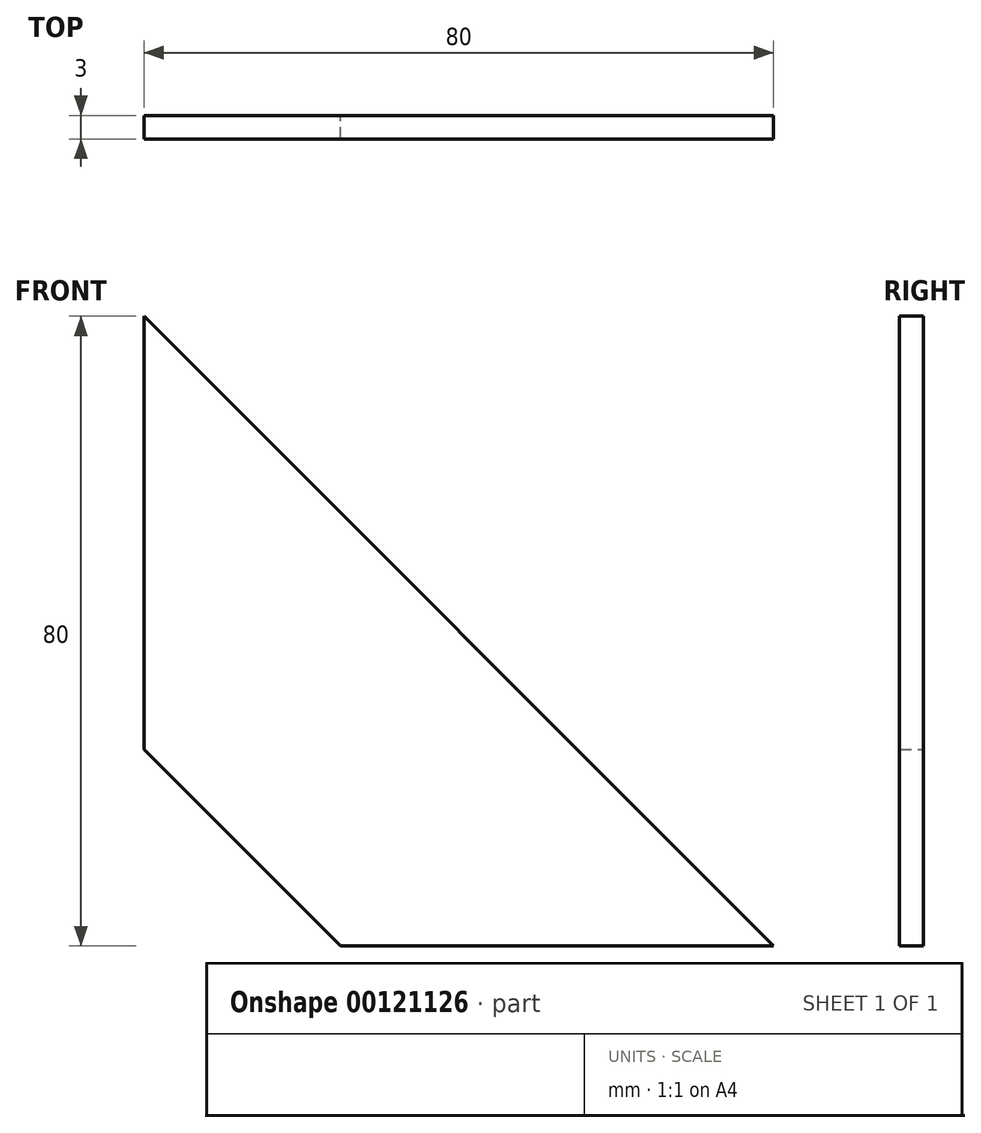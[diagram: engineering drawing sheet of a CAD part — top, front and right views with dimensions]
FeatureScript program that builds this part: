
annotation { "Feature Type Name" : "Feature", "Feature Type Description" : "" }
export const myFeature = defineFeature(function(context is Context, id is Id, definition is map)
    precondition{}
    {
        {
            var Q0;
            Q0=qCreatedBy(makeId("Front.planeOp"),FACE);
            var sketch = newSketch(context, id + "F0", { "sketchPlane" : qUnion([Q0])});
            skLineSegment(sketch, "E0.bottom", {"start": v(0, 0) * mm, "end": v(80, 0) * mm});
            skLineSegment(sketch, "E0.top", {"start": v(0, 80) * mm, "end": v(80, 80) * mm});
            skLineSegment(sketch, "E0.left", {"start": v(0, 0) * mm, "end": v(0, 80) * mm});
            skLineSegment(sketch, "E0.right", {"start": v(80, 0) * mm, "end": v(80, 80) * mm});
            skLineSegment(sketch, "E1", {"start": v(0, 80) * mm, "end": v(80, 0) * mm});
            skLineSegment(sketch, "E2", {"start": v(0, 25) * mm, "end": v(25, 0) * mm});
            skSolve(sketch);
        }
        {
            var Q0;
            {var subQ0=sQuery(id+"F0.wireOp",EDGE,"E1");Q0=makeQuery(id+"F0.imprint","IMPRINT",FACE,{"disambiguationData":[TD([[makeQuery(id+"F0.imprint","IMPRINT",EDGE,{"derivedFrom":subQ0}),-1.0]])]});}
            extrude(context, id + "F1", {"entities" : qUnion([Q0]), "endBound" : BoundingType.SYMMETRIC, "depth" : 3 * mm});
        }
    });
